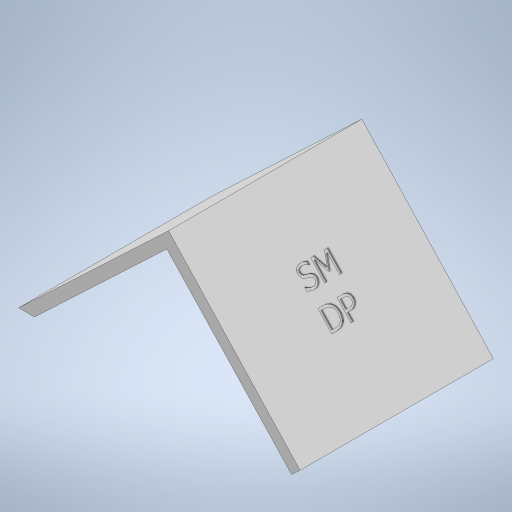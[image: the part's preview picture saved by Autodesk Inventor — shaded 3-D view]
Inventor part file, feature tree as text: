
AUTODESK INVENTOR PART (.ipt)
format: ipt  version: 2023 (Build 270158000, 158)  size: 330,752 bytes
history: native  units: in
note: dims shown in document units (in); Inventor stores cm internally (conversion verified against a paired STEP export)
features: extrude x2, sketch x2
ambient origin geometry x8: Origin, YZ Plane, XZ Plane, XY Plane, X Axis, Y Axis, Z Axis, Center Point
bodies: Solid1 (feature_tree)
feature tree (4):
  extrude  "Extrusion1"  Depth=11.8898in
  extrude  "Extrusion2"  Depth=0.6299in
  sketch  "Sketch1"  dims[d1=16.2205in d2=11.8898in]
  sketch  "Sketch2"  dims[d3=0.2981in d4=0.6299in d5=0.6693in d6=11.1417in d7=0.0in d8=0.0787in d9=0.0in]
